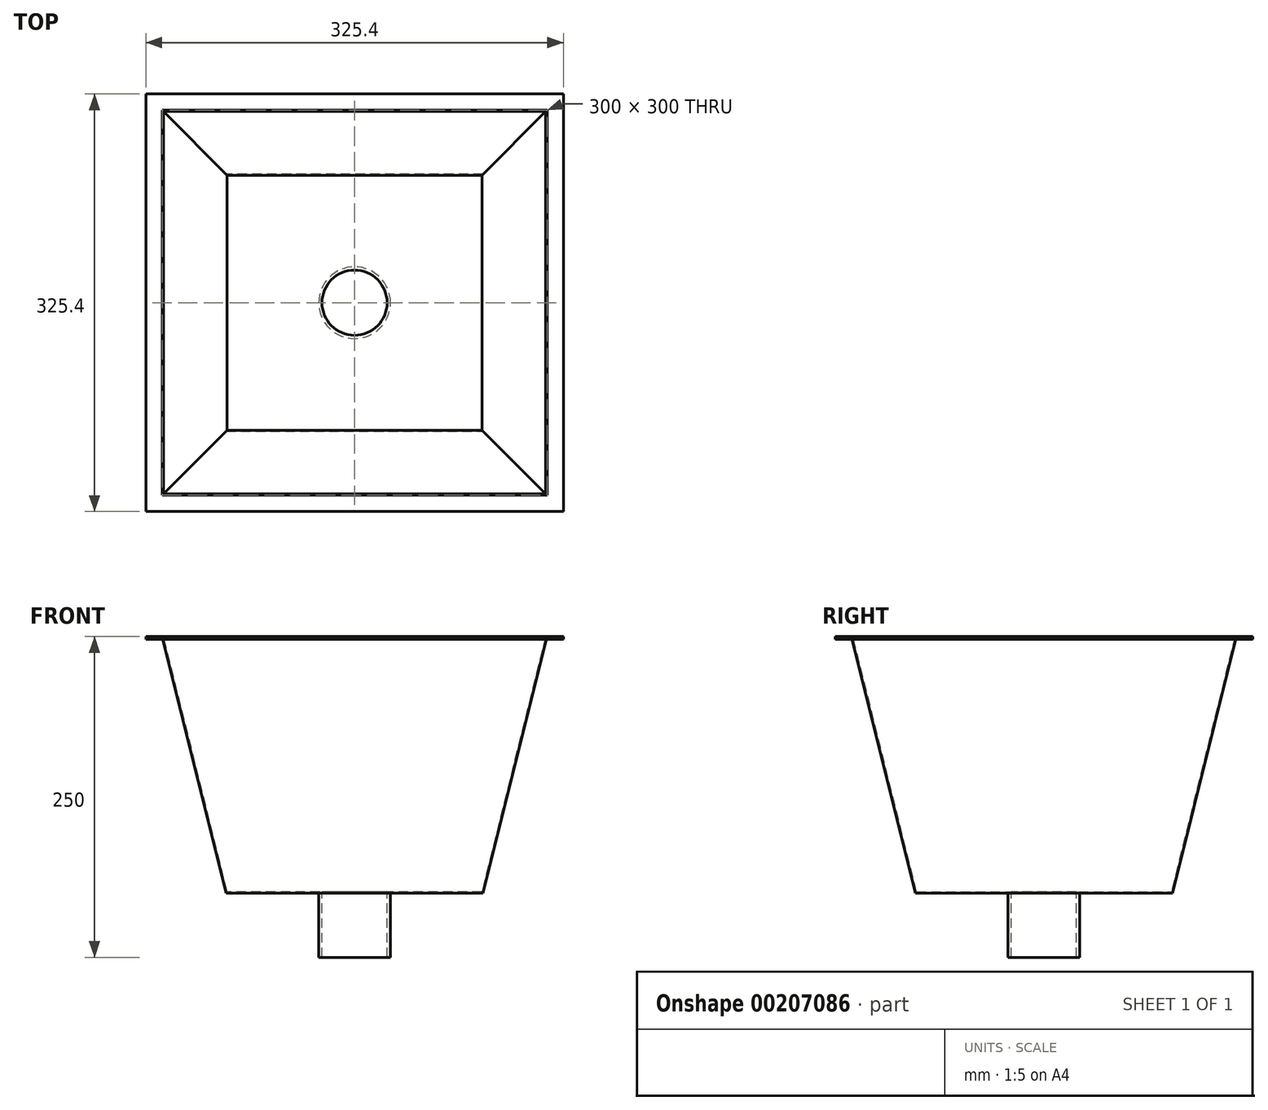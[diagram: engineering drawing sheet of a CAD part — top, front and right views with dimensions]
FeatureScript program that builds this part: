
annotation { "Feature Type Name" : "Feature", "Feature Type Description" : "" }
export const myFeature = defineFeature(function(context is Context, id is Id, definition is map)
    precondition{}
    {
        {
            var Q0;
            Q0=qCreatedBy(makeId("Top.planeOp"),FACE);
            var sketch = newSketch(context, id + "F0", { "sketchPlane" : qUnion([Q0])});
            skLineSegment(sketch, "E0.bottom", {"start": v(150, 150) * mm, "end": v(-150, 150) * mm});
            skLineSegment(sketch, "E0.top", {"start": v(150, -150) * mm, "end": v(-150, -150) * mm});
            skLineSegment(sketch, "E0.left", {"start": v(150, 150) * mm, "end": v(150, -150) * mm});
            skLineSegment(sketch, "E0.right", {"start": v(-150, 150) * mm, "end": v(-150, -150) * mm});
            skPoint(sketch, "E0.middle", {"position": v(0, 0) * mm});
            skSolve(sketch);
        }
        {
            var Q0;
            Q0=makeQuery(id+"F0.imprint","IMPRINT",FACE,{"disambiguationData":[TD([[makeQuery(id+"F0.imprint","IMPRINT",EDGE,{"derivedFrom":sQuery(id+"F0.wireOp",EDGE,"E0.bottom")}),1.0]])]});
            extrude(context, id + "F1", {"entities" : qUnion([Q0]), "oppositeDirection" : true, "depth" : 200 * mm, "hasDraft" : true, "draftAngle" : 14 * degree, "draftPullDirection" : true});
        }
        {
            var Q0;
            Q0=makeQuery(id+"F1.opExtrude","CAP_FACE",FACE,{"disambiguationData":[OSD([sQuery(id+"F0.wireOp",EDGE,"E0.bottom"),sQuery(id+"F0.wireOp",EDGE,"E0.top"),sQuery(id+"F0.wireOp",EDGE,"E0.left"),sQuery(id+"F0.wireOp",EDGE,"E0.right")])],"isStart":true});
            shell(context, id + "F2", {"entities" : qUnion([Q0]), "thickness" : 1 * mm});
        }
        {
            var Q0;
            Q0=makeQuery(id+"F2.opShell","OFFSET_FACE",FACE,{"disambiguationData":[OSD([sQuery(id+"F0.wireOp",EDGE,"E0.bottom"),sQuery(id+"F0.wireOp",EDGE,"E0.top"),sQuery(id+"F0.wireOp",EDGE,"E0.left"),sQuery(id+"F0.wireOp",EDGE,"E0.right")])]});
            var sketch = newSketch(context, id + "F3", { "sketchPlane" : qUnion([Q0])});
            skCircle(sketch, "E1", {"center": v(0, 0) * mm, "radius": 25.4 * mm});
            skSolve(sketch);
        }
        {
            var Q0;
            Q0=makeQuery(id+"F3.imprint","IMPRINT",FACE,{"disambiguationData":[TD([[makeQuery(id+"F3.imprint","IMPRINT",EDGE,{"derivedFrom":sQuery(id+"F3.wireOp",EDGE,"E1")}),1.0]])]});
            extrude(context, id + "F4", {"entities" : qUnion([Q0]), "operationType" : NewBodyOperationType.REMOVE, "oppositeDirection" : true, "depth" : 25 * mm});
        }
        {
            var Q0;
            Q0=makeQuery(id+"F1.opExtrude","CAP_FACE",FACE,{"disambiguationData":[OSD([sQuery(id+"F0.wireOp",EDGE,"E0.bottom"),sQuery(id+"F0.wireOp",EDGE,"E0.top"),sQuery(id+"F0.wireOp",EDGE,"E0.left"),sQuery(id+"F0.wireOp",EDGE,"E0.right")])],"isStart":false});
            var sketch = newSketch(context, id + "F5", { "sketchPlane" : qUnion([Q0])});
            skCircle(sketch, "E2", {"center": v(0, 0) * mm, "radius": 27.94 * mm});
            skCircle(sketch, "E3", {"center": v(0, 0) * mm, "radius": 25.4 * mm});
            skSolve(sketch);
        }
        {
            var Q0;
            Q0=makeQuery(id+"F5.imprint","IMPRINT",FACE,{"disambiguationData":[TD([[makeQuery(id+"F5.imprint","IMPRINT",EDGE,{"derivedFrom":sQuery(id+"F5.wireOp",EDGE,"E2")}),1.0]])]});
            extrude(context, id + "F6", {"entities" : qUnion([Q0]), "operationType" : NewBodyOperationType.ADD, "depth" : 50 * mm});
        }
        {
            var Q0;
            Q0=makeQuery(id+"F1.opExtrude","CAP_FACE",FACE,{"disambiguationData":[OSD([sQuery(id+"F0.wireOp",EDGE,"E0.bottom"),sQuery(id+"F0.wireOp",EDGE,"E0.top"),sQuery(id+"F0.wireOp",EDGE,"E0.left"),sQuery(id+"F0.wireOp",EDGE,"E0.right")])],"isStart":true});
            var sketch = newSketch(context, id + "F7", { "sketchPlane" : qUnion([Q0])});
            skLineSegment(sketch, "E4.bottom", {"start": v(-150, -150) * mm, "end": v(149, -150) * mm});
            skLineSegment(sketch, "E4.top", {"start": v(-150, 149) * mm, "end": v(149, 149) * mm});
            skLineSegment(sketch, "E4.left", {"start": v(-150, -150) * mm, "end": v(-150, 149) * mm});
            skLineSegment(sketch, "E4.right", {"start": v(149, -150) * mm, "end": v(149, 149) * mm});
            skPoint(sketch, "E4.middle", {"position": v(0, 0) * mm});
            skLineSegment(sketch, "E5.bottom", {"start": v(-162.7, -162.7) * mm, "end": v(162.7, -162.7) * mm});
            skLineSegment(sketch, "E5.top", {"start": v(-162.7, 162.7) * mm, "end": v(162.7, 162.7) * mm});
            skLineSegment(sketch, "E5.left", {"start": v(-162.7, -162.7) * mm, "end": v(-162.7, 162.7) * mm});
            skLineSegment(sketch, "E5.right", {"start": v(162.7, -162.7) * mm, "end": v(162.7, 162.7) * mm});
            skSolve(sketch);
        }
        {
            var Q0;
            Q0=makeQuery(id+"F7.imprint","IMPRINT",FACE,{"disambiguationData":[TD([[makeQuery(id+"F7.imprint","IMPRINT",EDGE,{"derivedFrom":sQuery(id+"F7.wireOp",EDGE,"E4.bottom")}),1.0]])]});
            extrude(context, id + "F8", {"entities" : qUnion([Q0]), "operationType" : NewBodyOperationType.ADD, "oppositeDirection" : true, "depth" : 2 * mm});
        }
    });
